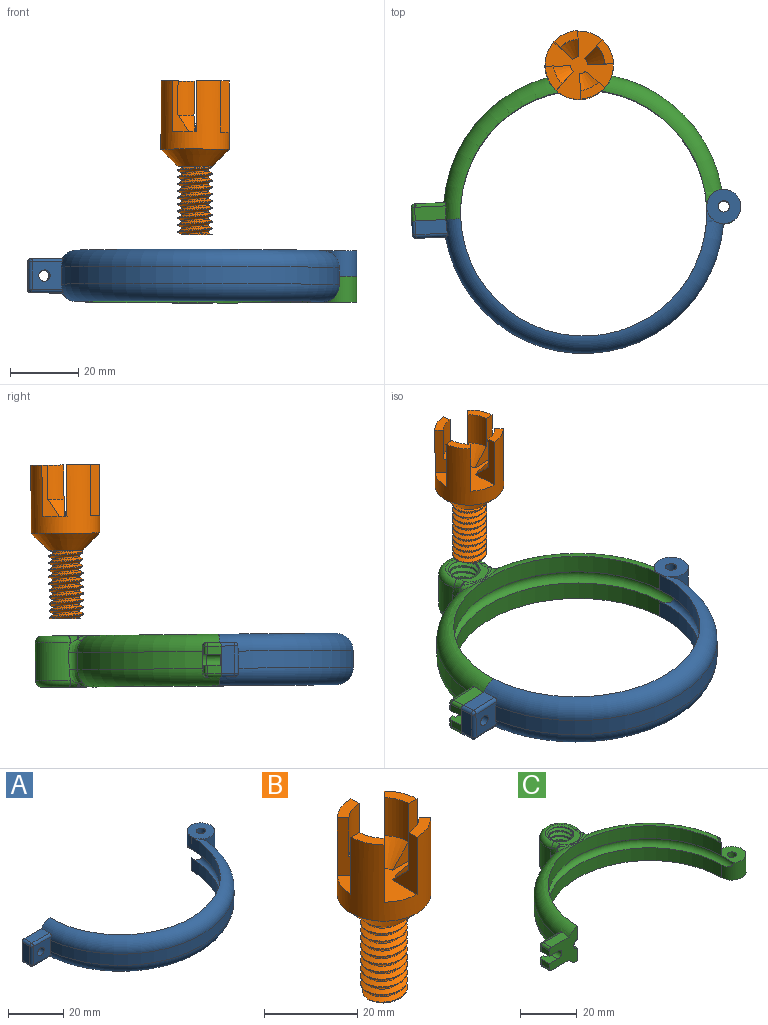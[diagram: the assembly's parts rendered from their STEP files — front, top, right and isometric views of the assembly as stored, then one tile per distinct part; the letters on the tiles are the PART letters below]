
ASSEMBLY  parts=3 mates=2
PART A: 24 faces, bbox 96.3x49.4x15 mm
  f0: cylinder r=41mm len=81.39mm, axis (0,0,1), area 593.9mm2, adj f1,f4,f10,f15,f16
  f1: cylinder r=5mm len=7.5mm, axis (0,0,1), area 46.6mm2, adj f0,f3,f8,f9,f16
  f2: cylinder r=36mm len=72mm, axis (0,0,1), area 622mm2, adj f4,f5,f9,f15
  f3: cylinder r=36mm len=72mm, axis (0,0,1), area 622mm2, adj f1,f5,f9,f16
  f4: cylinder r=5mm len=10mm, axis (0,0,1), area 180.2mm2, adj f0,f2,f6,f8,f9,f15
  f5: plane 15x14.3mm, normal (0,1,0), area 143.1mm2, adj f2,f3,f9,f11,f12,f13,f14,f15
  f6: plane 10.01x10.01mm, normal (0,0,1), area 70mm2, adj f4,f7
  f7: cylinder r=1.65mm len=7.5mm, axis (0,0,1), area 77.8mm2, adj f6,f8
  f8: plane 10x8.2mm, normal (0,0,-1), area 59.3mm2, adj f1,f4,f7,f9
  f9: torus R=36mm, axis (0,0,1), area 735.7mm2, adj f1,f2,f3,f4,f5,f8
  f10: plane 8.86x8.02mm, normal (0,-1,0), area 60.5mm2, adj f0,f13,f15,f16,f18,f20,f21
  f11: plane 9.17x4mm, normal (0,0,-1), area 36.1mm2, adj f5,f16,f21,f23
  f12: plane 8x4mm, normal (-1,0,0), area 32mm2, adj f5,f17,f20,f23
  f13: cylinder r=1.65mm len=5mm, axis (0,1,0), area 51.8mm2, adj f5,f10
  f14: plane 9.17x4mm, normal (0,0,1), area 36.1mm2, adj f5,f15,f17,f18
  f15: torus R=36mm, axis (0,0,-1), area 920.9mm2, adj f0,f2,f4,f5,f10,f14,f18
  f16: torus R=36mm, axis (0,0,-1), area 920.9mm2, adj f0,f1,f3,f5,f10,f11,f21
  f17: cylinder r=1mm len=4mm, axis (0,-1,0), area 6.3mm2, adj f5,f12,f14,f19
  f18: cylinder r=1mm len=9.17mm, axis (-1,0,0), area 14.1mm2, adj f10,f14,f15,f19
  f19: sphere r=1mm, area 1.6mm2, adj f17,f18,f20
  f20: cylinder r=1mm len=8mm, axis (0,0,-1), area 12.6mm2, adj f10,f12,f19,f22
  f21: cylinder r=1mm len=9.17mm, axis (1,0,0), area 14.1mm2, adj f10,f11,f16,f22
  f22: sphere r=1mm, area 1.6mm2, adj f20,f21,f23
  f23: cylinder r=1mm len=4mm, axis (0,1,0), area 6.3mm2, adj f5,f11,f12,f22
PART B: 32 faces, bbox 20.5x20.5x46.4 mm
  f0: cylinder r=5mm len=19.5mm, axis (0,0,-1), area 57.9mm2, adj f3,f28,f29,f31
  f1: plane 20x20mm, normal (0,0,1), area 166.9mm2, adj f4,f7,f8,f11,f12,f15,f16,f18
  f2: cylinder r=0.97mm len=25mm, axis (0,0,-1), area 153.2mm2, adj f3,f5
  f3: plane 9.38x9.33mm, normal (0,0,-1), area 57.7mm2, adj f0,f2,f27,f28,f29
  f4: cylinder r=10mm len=20mm, axis (0,0,-1), area 785.4mm2, adj f1,f7,f8,f9,f11,f12,f13,f15
  f5: plane 1.95x1.95mm, normal (0,0,-1), area 3mm2, adj f2
  f6: cylinder r=7.5mm len=10mm, axis (0,0,-1), area 58.9mm2, adj f7,f8,f9,f25
  f7: plane 15x7.5mm, normal (0,-1,0), area 50mm2, adj f1,f4,f6,f9,f25
  f8: plane 15x5.3mm, normal (-0.71,0.71,0), area 50mm2, adj f1,f4,f6,f9,f25
  f9: plane 7.07x4.7mm, normal (0,0,1), area 17.2mm2, adj f4,f6,f7,f8
  f10: cylinder r=7.5mm len=10mm, axis (0,0,-1), area 58.9mm2, adj f11,f12,f13,f24
  f11: plane 15x7.5mm, normal (1,0,0), area 50mm2, adj f1,f4,f10,f13,f24
  f12: plane 15x5.3mm, normal (-0.71,-0.71,0), area 50mm2, adj f1,f4,f10,f13,f24
  f13: plane 7.07x4.7mm, normal (0,0,1), area 17.2mm2, adj f4,f10,f11,f12
  f14: cylinder r=7.5mm len=10mm, axis (0,0,-1), area 58.9mm2, adj f15,f16,f17,f23
  f15: plane 15x7.5mm, normal (0,1,0), area 50mm2, adj f1,f4,f14,f17,f23
  f16: plane 15x5.3mm, normal (0.71,-0.71,0), area 50mm2, adj f1,f4,f14,f17,f23
  f17: plane 7.07x4.7mm, normal (0,0,1), area 17.2mm2, adj f4,f14,f15,f16
  f18: plane 15x5.3mm, normal (0.71,0.71,0), area 50mm2, adj f1,f4,f19,f21,f22
  f19: cylinder r=7.5mm len=10mm, axis (0,0,-1), area 58.9mm2, adj f18,f20,f21,f22
  f20: plane 15x7.5mm, normal (-1,0,0), area 50mm2, adj f1,f4,f19,f21,f22
  f21: plane 7.07x4.7mm, normal (0,0,1), area 17.2mm2, adj f4,f18,f19,f20
  f22: cone r=2.5mm half-angle=45deg, axis (0,0,1), area 27.8mm2, adj f1,f18,f19,f20
  f23: cone r=2.5mm half-angle=45deg, axis (0,0,1), area 27.8mm2, adj f1,f14,f15,f16
  f24: cone r=2.5mm half-angle=45deg, axis (0,0,1), area 27.8mm2, adj f1,f10,f11,f12
  f25: cone r=2.5mm half-angle=45deg, axis (0,0,1), area 27.8mm2, adj f1,f6,f7,f8
  f26: cone r=10mm half-angle=45deg, axis (0,0,1), area 333.2mm2, adj f4,f30
  f27: bspline ~21.5x9.05mm, area 135.6mm2, adj f3,f28,f29,f30
  f28: bspline ~21.63x11.55mm, area 345.7mm2, adj f0,f3,f27,f30,f31
  f29: bspline ~20.96x11.55mm, area 346.6mm2, adj f0,f3,f27,f30,f31
  f30: plane 10.06x10.06mm, normal (0,0,-1), area 29.3mm2, adj f26,f27,f28,f29,f31
  f31: cone r=5mm half-angle=63.4deg, axis (0,0,-1), area 12.7mm2, adj f0,f28,f29,f30
PART C: 65 faces, bbox 97.4x58.8x17.8 mm
  f0: plane 15x14.3mm, normal (0,-1,0), area 132.2mm2, adj f2,f5,f7,f8,f12,f13,f17,f18
  f1: plane 8.86x8.02mm, normal (0,1,0), area 35.8mm2, adj f3,f11,f12,f13,f20,f23,f24,f31
  f2: plane 4x2.35mm, normal (-1,0,0), area 9.4mm2, adj f0,f3,f21,f32
  f3: cylinder r=1mm len=2.35mm, axis (0,0,1), area 3.7mm2, adj f1,f2,f22,f32
  f4: plane 6.3x5.85mm, normal (0,1,0), area 17.1mm2, adj f5,f31,f32,f33
  f5: cylinder r=1.65mm len=4mm, axis (0,-1,0), area 22.2mm2, adj f0,f4,f32,f33
  f6: cylinder r=5mm len=7.5mm, axis (0,0,-1), area 46.6mm2, adj f8,f10,f13,f16,f30
  f7: cylinder r=36mm len=72mm, axis (0,0,-1), area 622mm2, adj f0,f9,f12,f30
  f8: cylinder r=36mm len=72mm, axis (0,0,-1), area 622mm2, adj f0,f6,f13,f30
  f9: cylinder r=5mm len=10mm, axis (0,0,-1), area 180.2mm2, adj f7,f10,f12,f14,f16,f30
  f10: cylinder r=41mm len=35.07mm, axis (0,0,-1), area 253mm2, adj f6,f9,f12,f13,f47
  f11: cylinder r=41mm len=35.06mm, axis (0,0,-1), area 252.9mm2, adj f1,f12,f13,f50
  f12: torus R=36mm, axis (0,0,1), area 812.5mm2, adj f0,f1,f7,f9,f10,f11,f17,f23
  f13: torus R=36mm, axis (0,0,1), area 812.5mm2, adj f0,f1,f6,f8,f10,f11,f18,f20
  f14: plane 10.01x10.01mm, normal (0,0,-1), area 51.9mm2, adj f9,f34,f35,f36,f37,f38,f39
  f15: cylinder r=1.65mm len=5.1mm, axis (0,0,-1), area 52.9mm2, adj f16,f40
  f16: plane 10x8.2mm, normal (0,0,1), area 59.3mm2, adj f6,f9,f15,f30
  f17: plane 9.17x4mm, normal (0,0,-1), area 36.1mm2, adj f0,f12,f23,f26
  f18: plane 9.17x4mm, normal (0,0,1), area 36.1mm2, adj f0,f13,f20,f21
  f19: plane 4x2.38mm, normal (-1,0,0), area 9.5mm2, adj f0,f24,f26,f33
  f20: cylinder r=1mm len=9.17mm, axis (1,0,0), area 14.1mm2, adj f1,f13,f18,f22
  f21: cylinder r=1mm len=4mm, axis (0,-1,0), area 6.3mm2, adj f0,f2,f18,f22
  f22: sphere r=1mm, area 2.1mm2, adj f3,f20,f21
  f23: cylinder r=1mm len=9.17mm, axis (-1,0,0), area 14.1mm2, adj f1,f12,f17,f25
  f24: cylinder r=1mm len=2.38mm, axis (0,0,1), area 3.7mm2, adj f1,f19,f25,f33
  f25: sphere r=1mm, area 2.1mm2, adj f23,f24,f26
  f26: cylinder r=1mm len=4mm, axis (0,1,0), area 6.3mm2, adj f0,f17,f19,f25
  f27: cylinder r=7.5mm len=15mm, axis (0,0,-1), area 306.1mm2, adj f45,f47,f48,f49,f50,f52,f57,f60
  f28: plane 13.42x11.56mm, normal (0,0,1), area 46.4mm2, adj f41,f42,f43,f44,f59,f60,f62,f63
  f29: plane 14x12.14mm, normal (0,0,-1), area 46.1mm2, adj f41,f42,f43,f44,f54,f55,f57,f58
  f30: torus R=36mm, axis (0,0,-1), area 735.7mm2, adj f0,f6,f7,f8,f9,f16
  f31: cylinder r=3.15mm len=6.3mm, axis (0,1,0), area 16.4mm2, adj f1,f4,f32,f33
  f32: plane 5x4.59mm, normal (0,0,-1), area 20.1mm2, adj f0,f1,f2,f3,f4,f5,f31
  f33: plane 5x4.35mm, normal (0,0,1), area 19.1mm2, adj f0,f1,f4,f5,f19,f24,f31
  f34: plane 3.2x2.4mm, normal (0,-1,0), area 7.7mm2, adj f14,f35,f39,f40
  f35: plane 2.78x2.4mm, normal (0.87,-0.5,0), area 7.7mm2, adj f14,f34,f36,f40
  f36: plane 2.78x2.4mm, normal (0.87,0.5,0), area 7.7mm2, adj f14,f35,f37,f40
  f37: plane 3.2x2.4mm, normal (0,1,0), area 7.7mm2, adj f14,f36,f38,f40
  f38: plane 2.78x2.4mm, normal (-0.87,0.5,0), area 7.7mm2, adj f14,f37,f39,f40
  f39: plane 2.78x2.4mm, normal (-0.87,-0.5,0), area 7.7mm2, adj f14,f34,f38,f40
  f40: plane 6.41x5.55mm, normal (0,0,-1), area 18.1mm2, adj f15,f34,f35,f36,f37,f38,f39
  f41: bspline ~16.29x12.08mm, area 278.2mm2, adj f28,f29,f43,f44
  f42: bspline ~16.63x12.08mm, area 275.8mm2, adj f28,f29,f43,f44
  f43: bspline ~15.92x12.29mm, area 72.3mm2, adj f28,f29,f41,f42
  f44: cylinder r=4.15mm len=15mm, axis (0,0,1), area 50.1mm2, adj f28,f29,f41,f42
  f45: bspline ~6.97x4.15mm, area 13.2mm2, adj f13,f27,f46,f47,f59
  f46: bspline ~16.41x4.77mm, area 17.8mm2, adj f13,f45,f48,f61,f63,f64
  f47: cylinder r=2mm len=5mm, axis (0,0,1), area 16.2mm2, adj f10,f27,f45,f49
  f48: bspline ~7.36x4.5mm, area 13.2mm2, adj f13,f27,f46,f50,f62
  f49: bspline ~7.36x4.5mm, area 13.2mm2, adj f12,f27,f47,f51,f58
  f50: cylinder r=2mm len=5mm, axis (0,0,-1), area 16.2mm2, adj f11,f27,f48,f52
  f51: bspline ~16.41x4.77mm, area 17.8mm2, adj f12,f49,f52,f53,f54,f56
  f52: bspline ~6.97x4.15mm, area 13.2mm2, adj f12,f27,f50,f51,f55
  f53: bspline ~1.74x1mm, area -1mm2, adj f51,f54,f55
  f54: bspline ~12.56x3.09mm, area 183mm2, adj f29,f51,f53,f56
  f55: bspline ~4.01x2.61mm, area 6.4mm2, adj f29,f52,f53,f57
  f56: bspline ~1.74x1mm, area 0.4mm2, adj f51,f54,f58
  f57: torus R=5.5mm, axis (0,0,1), area 81.2mm2, adj f27,f29,f55,f58
  f58: bspline ~4.09x2.61mm, area 6.4mm2, adj f29,f49,f56,f57
  f59: bspline ~4.01x2.61mm, area 6.4mm2, adj f28,f45,f60,f61
  f60: torus R=5.5mm, axis (0,0,1), area 81.2mm2, adj f27,f28,f59,f62
  f61: bspline ~1.74x1mm, area 0.4mm2, adj f46,f59,f63
  f62: bspline ~4.09x2.61mm, area 6.4mm2, adj f28,f48,f60,f64
  f63: bspline ~12.56x3.09mm, area 5.6mm2, adj f28,f46,f61,f64
  f64: bspline ~1.74x1mm, area 0.4mm2, adj f46,f62,f63
PLACE A rot(axis=(-0.2,0.05,0.98),2.7deg) t=(0.04,7.1,114.96)mm
PLACE B rot(axis=(0,0,-1),177.3deg) t=(-1.35,49.93,119.56)mm
PLACE C rot(axis=(-0.2,0.05,0.98),2.7deg) t=(0,6.96,99.96)mm fixed
MATE revolute C.f6 <-> A.f4  axis (0,-0.01,-1) through (40.97,8.95,107.36)mm
MATE cylindrical B.f2 <-> C.f28  axis (0,0.01,1) through (-1.35,49.93,119.56)mm
